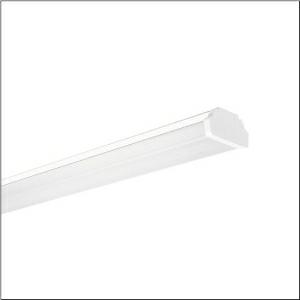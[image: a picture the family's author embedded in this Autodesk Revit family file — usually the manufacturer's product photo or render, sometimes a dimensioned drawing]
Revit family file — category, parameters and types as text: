
# Revit family: dus_r__31_ho_53bd812c1v4105_1de4
name_source: partatom
category: Lighting Fixtures
units: mm (PartAtom-declared; Revit-internal decimal feet)

## family parameters
Cut with Voids When Loaded = No
Host = Face
Light Source = No
Part Type = Normal
Room Calculation Point = No
Round Connector Dimension = Use Diameter
Shared = No

## types (1)
- --- (1 x LED, 10520 lm, 63.8 W, 4000K)
    Apparent Load = 64 VA
    CIE Flux Codes = 47 80 95 92 100
    Color Rendering = 80
    Color Temperature = 4000K
    Default Elevation = 1800 mm
    Description = DUS® 31 HOluminaire insert, length: 1.535mm, width: 81mm, height: 90mm, LED rated luminous flux: 10.520lm, light colour: 840, control gear: ON/OFF Multilumen, CLOi, control gear: ECG Multilumen, with plug, 3-pole, with phase selection, mains connection: 220..240V, AC, 50/60Hz, primary optical cover: cover, of PMMA, light emission: direct distribution, primary light characteristic: symmetric, protection rating (complete): IP20, protection rating (LED compartment): IP50, insulation class (complete): insulation class I (protective earthing), certification: CE, ENEC, VDE, UKCA, permissible ambient temperature for indoor applications: -35..+35°C, corresponds to IFS (International Featured Standards) requirements for safety and quality in the food industry, reducing of maximum allowable ambient temperature of 5°C with ceiling mounting, packaging unit: 1 piece
    Height = 95 mm
    Lamp = 1 x LED
    Lamp Light Flux = 10520 lm
    Lamp Power = 63.8 W
    Lamp count = 1
    Length = 1535 mm
    Luminous efficacy = 165 lm/W
    Manufacturer = Siteco
    ModVariant = No
    Model = 53BD812C1V4105
    Mounting Place = Ceiling
    Mounting Type = Pendant
    Number of Poles = 1
    OnlyDefault = Yes
    Power Factor = 1
    Product Name = DUS® 31 HO
    Product group = luminaire insert
    ProductGroupID = 902
    Protection Class = Protection class I
    Protection Degree = IP 20
    RLX_Detail_Level = 1
    RlxData = <blob elided: 39689 chars, md5=b9440dec>
    Socket = socket
    Standby Power = 0 W
    System Light Flux = 10520 lm
    System Power = 64 W
    Type Comments = factory setting: luminous flux: 100 % | (A | C | E) | 144 mA
    Type Image = l_1003451.jpg
    URL = http://relux.com
    VarID = @adj_131269
    Voltage = 0 V
    Weight = 0.00 kg
    Width = 81 mm

## geometry (parser evidence)
native form markers: Blend x4, Sweep x13
no freeform markers — native parametric forms only
